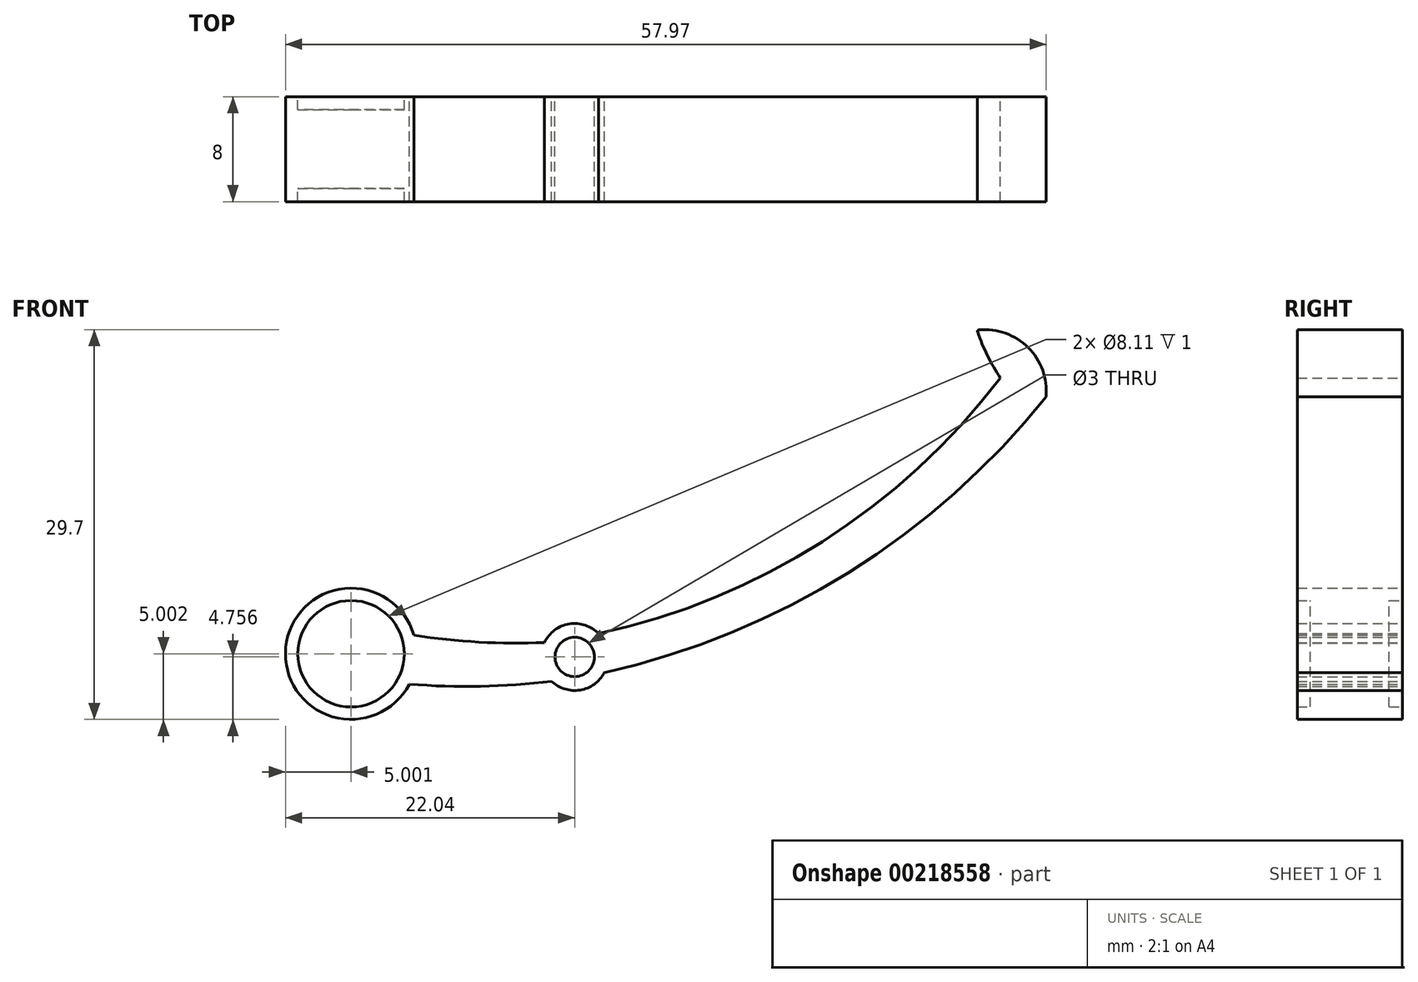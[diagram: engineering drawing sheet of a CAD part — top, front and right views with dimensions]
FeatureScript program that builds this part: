
annotation { "Feature Type Name" : "Feature", "Feature Type Description" : "" }
export const myFeature = defineFeature(function(context is Context, id is Id, definition is map)
    precondition{}
    {
        {
            var Q0;
            Q0=qCreatedBy(makeId("Front.planeOp"),FACE);
            var sketch = newSketch(context, id + "F0", { "sketchPlane" : qUnion([Q0])});
            skCircle(sketch, "E0", {"center": v(0, -69.95) * mm, "radius": 1.5 * mm});
            skPoint(sketch, "E1.visualSharp", {"position": v(32.48, -48.77) * mm});
            skArc(sketch, "E2", {"start": v(35.91, -50.13) * mm, "mid": v(34.55, -46.38) * mm, "end": v(30.79, -45.03) * mm});
            skArc(sketch, "E3", {"start": v(30.7, -45.18) * mm, "mid": v(31.45, -47) * mm, "end": v(32.43, -48.7) * mm});
            skArc(sketch, "E4.filletArc", {"start": v(30.79, -45.03) * mm, "mid": v(30.7, -45.08) * mm, "end": v(30.7, -45.18) * mm});
            skArc(sketch, "E5", {"start": v(-12.24, -68.3) * mm, "mid": v(-7.29, -68.82) * mm, "end": v(-2.3, -68.86) * mm});
            skArc(sketch, "E6", {"start": v(-12.6, -72.02) * mm, "mid": v(-7.18, -72.19) * mm, "end": v(-1.76, -71.8) * mm});
            skArc(sketch, "E7", {"start": v(1.83, -68.18) * mm, "mid": v(-0.41, -67.44) * mm, "end": v(-2.3, -68.86) * mm});
            skArc(sketch, "E8.trimOffspring", {"start": v(1.83, -68.18) * mm, "mid": v(18.87, -61.17) * mm, "end": v(32.43, -48.7) * mm});
            skArc(sketch, "E9.trimOffspring", {"start": v(2.26, -71.15) * mm, "mid": v(20.88, -63.52) * mm, "end": v(35.91, -50.13) * mm});
            skArc(sketch, "E10.trimOffspring", {"start": v(-1.76, -71.8) * mm, "mid": v(0.41, -72.47) * mm, "end": v(2.26, -71.15) * mm});
            skPoint(sketch, "E11.orphan", {"position": v(-17.75, -71.35) * mm});
            skArc(sketch, "E12", {"start": v(-12.24, -68.3) * mm, "mid": v(-22.02, -69.23) * mm, "end": v(-12.6, -72.02) * mm});
            skPoint(sketch, "E13.orphan", {"position": v(-8.68, -68.72) * mm});
            skCircle(sketch, "E14", {"center": v(-17.04, -69.7) * mm, "radius": 4.05 * mm});
            skSolve(sketch);
        }
        {
            var Q0;
            {var subQ0=sQuery(id+"F0.wireOp",EDGE,"E12");Q0=makeQuery(id+"F0.imprint","IMPRINT",FACE,{"disambiguationData":[TD([[makeQuery(id+"F0.imprint","IMPRINT",EDGE,{"derivedFrom":subQ0}),-1.0]])]});}
            var Q1;
            Q1=makeQuery(id+"F0.imprint","IMPRINT",FACE,{"disambiguationData":[TD([[makeQuery(id+"F0.imprint","IMPRINT",EDGE,{"derivedFrom":sQuery(id+"F0.wireOp",EDGE,"E0")}),-1.0]])]});
            extrude(context, id + "F1", {"entities" : qUnion([Q0, Q1]), "depth" : 5 * mm, "symmetric" : true});
        }
        {
            var Q0;
            {var subQ0=sQuery(id+"F0.wireOp",EDGE,"E12");Q0=makeQuery(id+"F0.imprint","IMPRINT",FACE,{"disambiguationData":[TD([[makeQuery(id+"F0.imprint","IMPRINT",EDGE,{"derivedFrom":subQ0}),1.0]])]});}
            extrude(context, id + "F2", {"entities" : qUnion([Q0]), "operationType" : NewBodyOperationType.ADD, "depth" : 8 * mm, "symmetric" : true});
        }
        {
            var Q0;
            Q0=makeQuery(id+"F0.imprint","IMPRINT",FACE,{"disambiguationData":[TD([[makeQuery(id+"F0.imprint","IMPRINT",EDGE,{"derivedFrom":sQuery(id+"F0.wireOp",EDGE,"E14")}),1.0]])]});
            extrude(context, id + "F3", {"entities" : qUnion([Q0]), "operationType" : NewBodyOperationType.ADD, "depth" : 6 * mm, "symmetric" : true});
        }
    });
